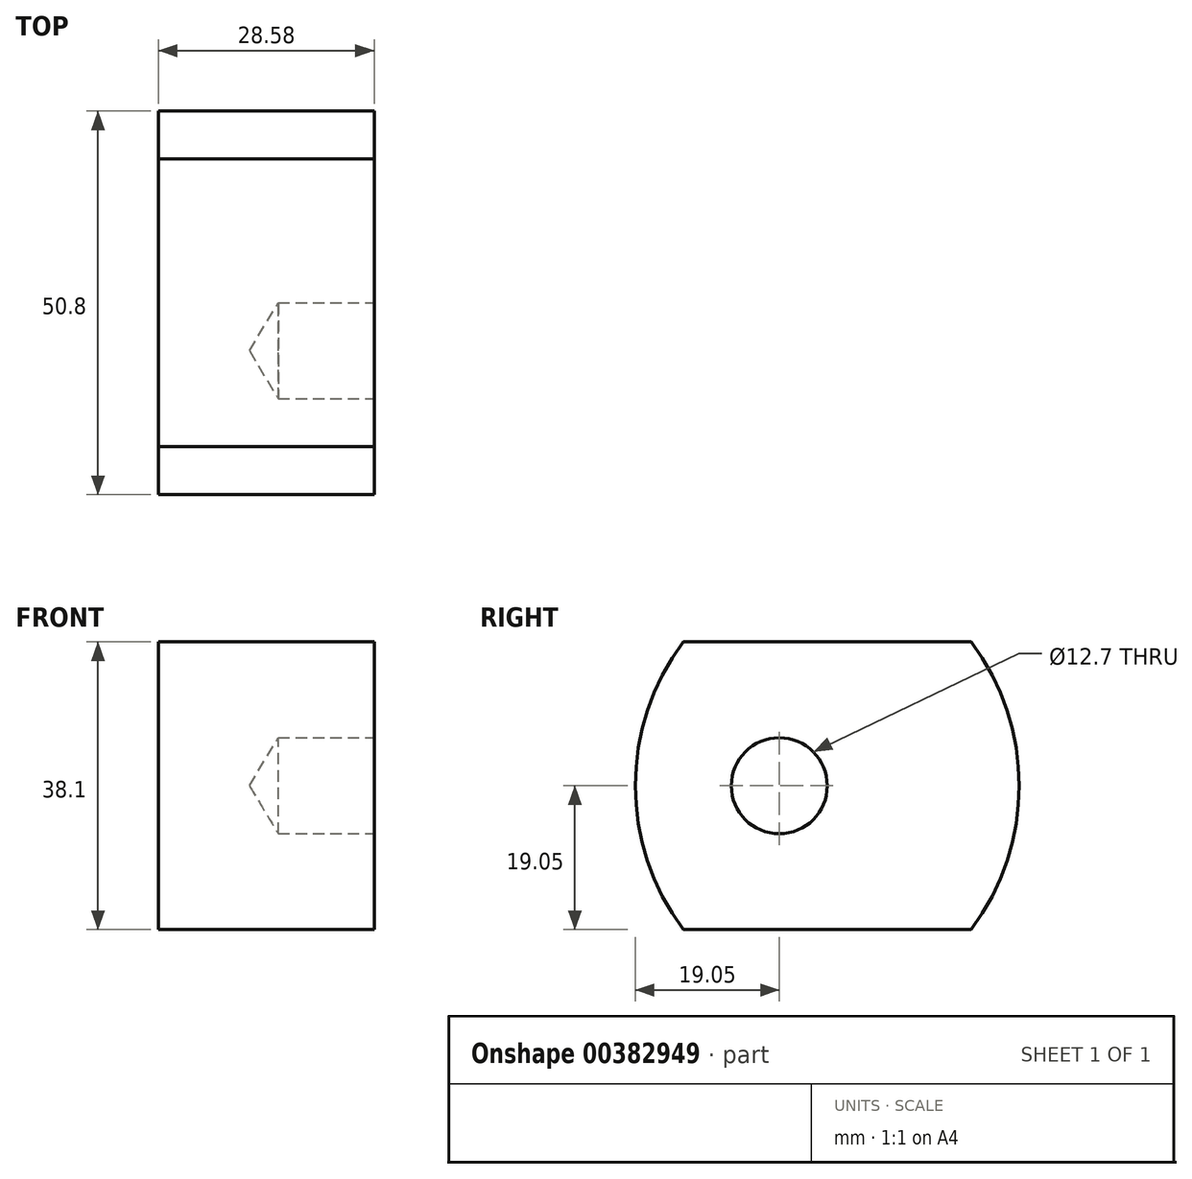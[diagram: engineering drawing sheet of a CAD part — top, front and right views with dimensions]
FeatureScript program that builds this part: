
annotation { "Feature Type Name" : "Feature", "Feature Type Description" : "" }
export const myFeature = defineFeature(function(context is Context, id is Id, definition is map)
    precondition{}
    {
        {
            var Q0;
            Q0=qCreatedBy(makeId("Top.planeOp"),FACE);
            var sketch = newSketch(context, id + "F0", { "sketchPlane" : qUnion([Q0])});
            skLineSegment(sketch, "E0.bottom", {"start": v(14.29, 19.05) * mm, "end": v(-14.29, 19.05) * mm});
            skLineSegment(sketch, "E0.top", {"start": v(14.29, -19.05) * mm, "end": v(-14.29, -19.05) * mm});
            skLineSegment(sketch, "E0.left", {"start": v(14.29, 19.05) * mm, "end": v(14.29, -19.05) * mm});
            skLineSegment(sketch, "E0.right", {"start": v(-14.29, 19.05) * mm, "end": v(-14.29, -19.05) * mm});
            skPoint(sketch, "E0.middle", {"position": v(0, 0) * mm});
            skSolve(sketch);
        }
        {
            var Q0;
            Q0=makeQuery(id+"F0.imprint","IMPRINT",FACE,{"disambiguationData":[TD([[makeQuery(id+"F0.imprint","IMPRINT",EDGE,{"derivedFrom":sQuery(id+"F0.wireOp",EDGE,"E0.bottom")}),1.0]])]});
            extrude(context, id + "F1", {"entities" : qUnion([Q0]), "depth" : 38.1 * mm});
        }
        {
            var Q0;
            Q0=makeQuery(id+"F1.opExtrude","SWEPT_FACE",FACE,{"disambiguationData":[OSD([sQuery(id+"F0.wireOp",EDGE,"E0.left")])]});
            var sketch = newSketch(context, id + "F2", { "sketchPlane" : qUnion([Q0])});
            skArc(sketch, "E1", {"start": v(19.05, 0) * mm, "mid": v(25.4, 19.05) * mm, "end": v(19.05, 38.1) * mm});
            skArc(sketch, "E2", {"start": v(-19.05, 38.1) * mm, "mid": v(-25.4, 19.05) * mm, "end": v(-19.05, 0) * mm});
            skSolve(sketch);
        }
        {
            var Q0;
            Q0=makeQuery(id+"F2.imprint","IMPRINT",FACE,{"disambiguationData":[TD([[makeQuery(id+"F2.imprint","IMPRINT",EDGE,{"derivedFrom":sQuery(id+"F2.wireOp",EDGE,"E2")}),1.0]])]});
            var Q1;
            Q1=makeQuery(id+"F2.imprint","IMPRINT",FACE,{"disambiguationData":[TD([[makeQuery(id+"F2.imprint","IMPRINT",EDGE,{"derivedFrom":sQuery(id+"F2.wireOp",EDGE,"E1")}),1.0]])]});
            var Q2;
            Q2=makeQuery(id+"F1.opExtrude","SWEPT_FACE",FACE,{"disambiguationData":[OSD([sQuery(id+"F0.wireOp",EDGE,"E0.right")])]});
            extrude(context, id + "F3", {"entities" : qUnion([Q0, Q1]), "operationType" : NewBodyOperationType.ADD, "endBound" : BoundingType.UP_TO_SURFACE, "oppositeDirection" : true, "endBoundEntityFace" : qUnion([Q2]), "depth" : 25.4 * mm});
        }
        {
            var Q0;
            Q0=sQuery(id+"F2.wireOp",VERTEX,"E1.center");
            var Q1;
            Q1=makeQuery(id+"F1.opExtrude","SWEPT_BODY",BODY,{"disambiguationData":[OSD([sQuery(id+"F0.wireOp",EDGE,"E0.bottom"),sQuery(id+"F0.wireOp",EDGE,"E0.top"),sQuery(id+"F0.wireOp",EDGE,"E0.left"),sQuery(id+"F0.wireOp",EDGE,"E0.right")])]});
            hole(context, id + "F4", {"style" : HoleStyle.SIMPLE, "endStyle" : HoleEndStyle.BLIND, "holeDiameter" : 12.7 * mm, "holeDepth" : 12.7 * mm, "isTappedThrough" : true, "tappedDepth" : 12.7 * mm, "tapClearance" : 3, "startFromSketch" : true, "locations" : qUnion([Q0]), "scope" : qUnion([Q1])});
        }
    });
